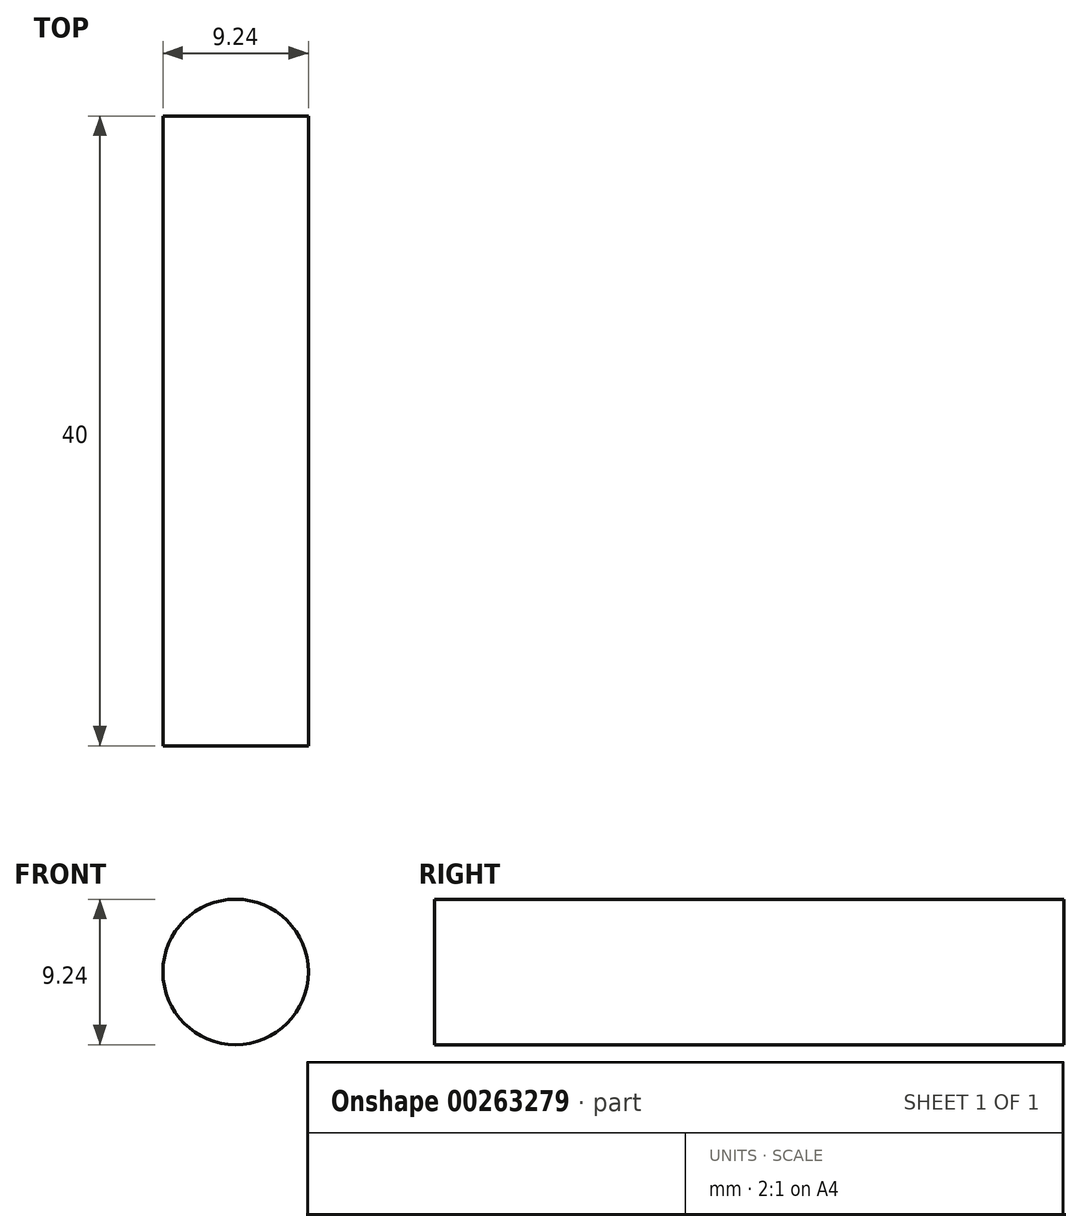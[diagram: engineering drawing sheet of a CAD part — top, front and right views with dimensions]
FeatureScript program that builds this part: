
annotation { "Feature Type Name" : "Feature", "Feature Type Description" : "" }
export const myFeature = defineFeature(function(context is Context, id is Id, definition is map)
    precondition{}
    {
        {
            var Q0;
            Q0=qCreatedBy(makeId("Front.planeOp"),FACE);
            var sketch = newSketch(context, id + "F0", { "sketchPlane" : qUnion([Q0])});
            skCircle(sketch, "E0", {"center": v(0, 0) * mm, "radius": 4.62 * mm});
            skSolve(sketch);
        }
        {
            var Q0;
            Q0 = qSketchRegion(id + "F0", true);
            extrude(context, id + "F1", {"entities" : qUnion([Q0]), "depth" : 40 * mm});
        }
    });
